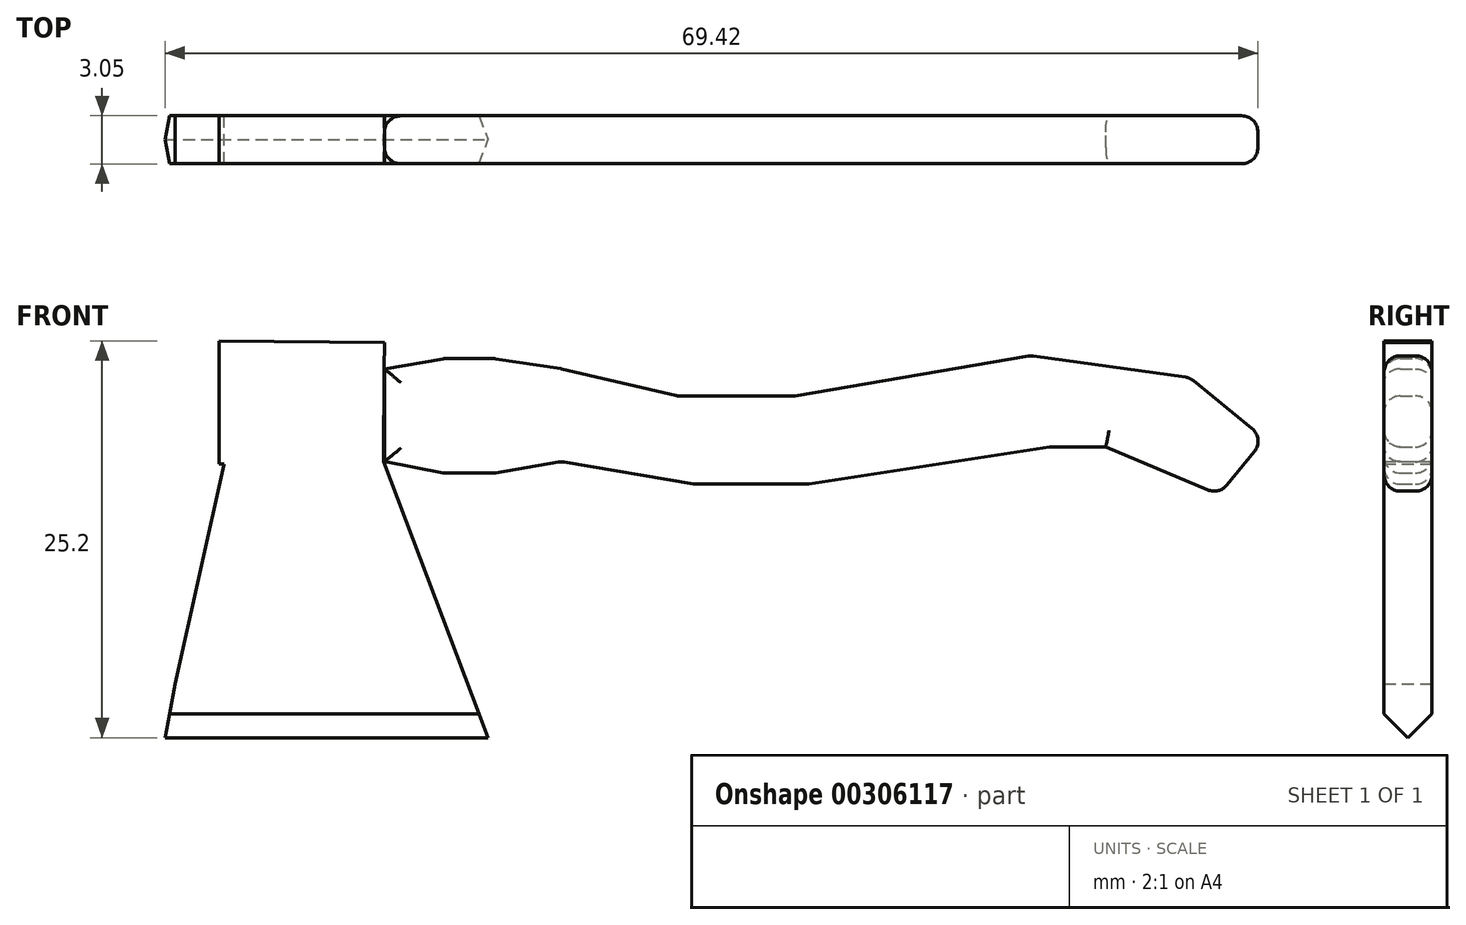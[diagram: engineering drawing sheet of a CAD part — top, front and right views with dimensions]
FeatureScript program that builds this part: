
annotation { "Feature Type Name" : "Feature", "Feature Type Description" : "" }
export const myFeature = defineFeature(function(context is Context, id is Id, definition is map)
    precondition{}
    {
        {
            var Q0;
            Q0=qCreatedBy(makeId("Front.planeOp"),FACE);
            var sketch = newSketch(context, id + "F0", { "sketchPlane" : qUnion([Q0])});
            skLineSegment(sketch, "E0", {"start": v(11.94, 3.92) * mm, "end": v(4.74, 6.95) * mm});
            skLineSegment(sketch, "E1", {"start": v(4.74, 6.95) * mm, "end": v(1.23, 6.95) * mm});
            skLineSegment(sketch, "E2", {"start": v(1.23, 6.95) * mm, "end": v(-14.2, 4.59) * mm});
            skLineSegment(sketch, "E3", {"start": v(-14.2, 4.59) * mm, "end": v(-21.36, 4.59) * mm});
            skLineSegment(sketch, "E4", {"start": v(-21.36, 4.59) * mm, "end": v(-29.85, 6.01) * mm});
            skLineSegment(sketch, "E5", {"start": v(-29.85, 6.01) * mm, "end": v(-34.1, 5.3) * mm});
            skLineSegment(sketch, "E6", {"start": v(-34.1, 5.3) * mm, "end": v(-37.26, 5.3) * mm});
            skLineSegment(sketch, "E7", {"start": v(-37.26, 5.3) * mm, "end": v(-41.07, 6.01) * mm});
            skLineSegment(sketch, "E8", {"start": v(-41.07, 6.01) * mm, "end": v(-41.07, 11.91) * mm});
            skLineSegment(sketch, "E9", {"start": v(-41.07, 11.91) * mm, "end": v(-37.26, 12.56) * mm});
            skLineSegment(sketch, "E10", {"start": v(-37.26, 12.56) * mm, "end": v(-34.1, 12.56) * mm});
            skLineSegment(sketch, "E11", {"start": v(-34.1, 12.56) * mm, "end": v(-29.85, 11.91) * mm});
            skLineSegment(sketch, "E12", {"start": v(-29.85, 11.91) * mm, "end": v(-22.44, 10.18) * mm});
            skLineSegment(sketch, "E13", {"start": v(-22.44, 10.18) * mm, "end": v(-15.1, 10.18) * mm});
            skLineSegment(sketch, "E14", {"start": v(-15.1, 10.18) * mm, "end": v(0, 12.75) * mm});
            skLineSegment(sketch, "E15", {"start": v(11.94, 3.92) * mm, "end": v(14.83, 7.45) * mm});
            skLineSegment(sketch, "E16", {"start": v(14.83, 7.45) * mm, "end": v(10.08, 11.34) * mm});
            skLineSegment(sketch, "E17", {"start": v(10.08, 11.34) * mm, "end": v(0, 12.75) * mm});
            skLineSegment(sketch, "E18", {"start": v(-41.09, 11.91) * mm, "end": v(-41.07, 13.58) * mm});
            skLineSegment(sketch, "E19", {"start": v(-41.07, 13.58) * mm, "end": v(-51.58, 13.68) * mm});
            skLineSegment(sketch, "E20", {"start": v(-51.58, 13.68) * mm, "end": v(-51.58, 5.88) * mm});
            skLineSegment(sketch, "E21", {"start": v(-51.58, 5.88) * mm, "end": v(-51.25, 5.88) * mm});
            skLineSegment(sketch, "E22", {"start": v(-51.25, 5.88) * mm, "end": v(-54.38, -8.11) * mm});
            skLineSegment(sketch, "E23", {"start": v(-54.38, -8.11) * mm, "end": v(-55.2, -12.54) * mm});
            skLineSegment(sketch, "E24", {"start": v(-55.2, -12.54) * mm, "end": v(-34.1, -12.54) * mm});
            skLineSegment(sketch, "E25", {"start": v(-34.1, -12.54) * mm, "end": v(-41.14, 6.01) * mm});
            skLineSegment(sketch, "E26", {"start": v(-41.14, 6.01) * mm, "end": v(-41.09, 11.91) * mm});
            skSolve(sketch);
        }
        {
            var Q0;
            Q0 = qSketchRegion(id + "F0", true);
            extrude(context, id + "F1", {"entities" : qUnion([Q0]), "depth" : 3.05 * mm});
        }
        {
            var Q0;
            Q0=makeQuery(id+"F1.opExtrude","CAP_EDGE",EDGE,{"disambiguationData":[OSD([sQuery(id+"F0.wireOp",EDGE,"E15")])],"isStart":false});
            var Q1;
            Q1=makeQuery(id+"F1.opExtrude","CAP_EDGE",EDGE,{"disambiguationData":[OSD([sQuery(id+"F0.wireOp",EDGE,"E15")])],"isStart":true});
            var Q2;
            Q2=makeQuery(id+"F1.opExtrude","CAP_EDGE",EDGE,{"disambiguationData":[OSD([sQuery(id+"F0.wireOp",EDGE,"E16")])],"isStart":true});
            var Q3;
            Q3=makeQuery(id+"F1.opExtrude","CAP_EDGE",EDGE,{"disambiguationData":[OSD([sQuery(id+"F0.wireOp",EDGE,"E16")])],"isStart":false});
            var Q4;
            Q4=makeQuery(id+"F1.opExtrude","SWEPT_EDGE",EDGE,{"disambiguationData":[OSD([sQuery(id+"F0.wireOp",EDGE,"E15"),sQuery(id+"F0.wireOp",EDGE,"E16")])]});
            var Q5;
            Q5=makeQuery(id+"F1.opExtrude","SWEPT_EDGE",EDGE,{"disambiguationData":[OSD([sQuery(id+"F0.wireOp",EDGE,"E0"),sQuery(id+"F0.wireOp",EDGE,"E15")])]});
            var Q6;
            Q6=makeQuery(id+"F1.opExtrude","CAP_EDGE",EDGE,{"disambiguationData":[OSD([sQuery(id+"F0.wireOp",EDGE,"E0")])],"isStart":false});
            var Q7;
            Q7=makeQuery(id+"F1.opExtrude","CAP_EDGE",EDGE,{"disambiguationData":[OSD([sQuery(id+"F0.wireOp",EDGE,"E1")])],"isStart":false});
            var Q8;
            Q8=makeQuery(id+"F1.opExtrude","CAP_EDGE",EDGE,{"disambiguationData":[OSD([sQuery(id+"F0.wireOp",EDGE,"E2")])],"isStart":false});
            var Q9;
            Q9=makeQuery(id+"F1.opExtrude","CAP_EDGE",EDGE,{"disambiguationData":[OSD([sQuery(id+"F0.wireOp",EDGE,"E14")])],"isStart":false});
            var Q10;
            Q10=makeQuery(id+"F1.opExtrude","CAP_EDGE",EDGE,{"disambiguationData":[OSD([sQuery(id+"F0.wireOp",EDGE,"E17")])],"isStart":false});
            var Q11;
            Q11=makeQuery(id+"F1.opExtrude","CAP_EDGE",EDGE,{"disambiguationData":[OSD([sQuery(id+"F0.wireOp",EDGE,"E17")])],"isStart":true});
            var Q12;
            Q12=makeQuery(id+"F1.opExtrude","SWEPT_EDGE",EDGE,{"disambiguationData":[OSD([sQuery(id+"F0.wireOp",EDGE,"E14"),sQuery(id+"F0.wireOp",EDGE,"E17")])]});
            var Q13;
            Q13=makeQuery(id+"F1.opExtrude","SWEPT_EDGE",EDGE,{"disambiguationData":[OSD([sQuery(id+"F0.wireOp",EDGE,"E16"),sQuery(id+"F0.wireOp",EDGE,"E17")])]});
            var Q14;
            Q14=makeQuery(id+"F1.opExtrude","SWEPT_FACE",FACE,{"disambiguationData":[OSD([sQuery(id+"F0.wireOp",EDGE,"E4")])]});
            var Q15;
            Q15=makeQuery(id+"F1.opExtrude","SWEPT_FACE",FACE,{"disambiguationData":[OSD([sQuery(id+"F0.wireOp",EDGE,"E3")])]});
            var Q16;
            Q16=makeQuery(id+"F1.opExtrude","SWEPT_FACE",FACE,{"disambiguationData":[OSD([sQuery(id+"F0.wireOp",EDGE,"E2")])]});
            var Q17;
            Q17=makeQuery(id+"F1.opExtrude","SWEPT_FACE",FACE,{"disambiguationData":[OSD([sQuery(id+"F0.wireOp",EDGE,"E6")])]});
            var Q18;
            Q18=makeQuery(id+"F1.opExtrude","CAP_FACE",FACE,{"disambiguationData":[OSD([sQuery(id+"F0.wireOp",EDGE,"E0"),sQuery(id+"F0.wireOp",EDGE,"E1"),sQuery(id+"F0.wireOp",EDGE,"E2"),sQuery(id+"F0.wireOp",EDGE,"E3"),sQuery(id+"F0.wireOp",EDGE,"E4"),sQuery(id+"F0.wireOp",EDGE,"E5"),sQuery(id+"F0.wireOp",EDGE,"E6"),sQuery(id+"F0.wireOp",EDGE,"E7"),sQuery(id+"F0.wireOp",EDGE,"E8"),sQuery(id+"F0.wireOp",EDGE,"E9"),sQuery(id+"F0.wireOp",EDGE,"E10"),sQuery(id+"F0.wireOp",EDGE,"E11"),sQuery(id+"F0.wireOp",EDGE,"E12"),sQuery(id+"F0.wireOp",EDGE,"E13"),sQuery(id+"F0.wireOp",EDGE,"E14"),sQuery(id+"F0.wireOp",EDGE,"E15"),sQuery(id+"F0.wireOp",EDGE,"E16"),sQuery(id+"F0.wireOp",EDGE,"E17")])],"isStart":false});
            var Q19;
            Q19=makeQuery(id+"F1.opExtrude","CAP_FACE",FACE,{"disambiguationData":[OSD([sQuery(id+"F0.wireOp",EDGE,"E0"),sQuery(id+"F0.wireOp",EDGE,"E1"),sQuery(id+"F0.wireOp",EDGE,"E2"),sQuery(id+"F0.wireOp",EDGE,"E3"),sQuery(id+"F0.wireOp",EDGE,"E4"),sQuery(id+"F0.wireOp",EDGE,"E5"),sQuery(id+"F0.wireOp",EDGE,"E6"),sQuery(id+"F0.wireOp",EDGE,"E7"),sQuery(id+"F0.wireOp",EDGE,"E8"),sQuery(id+"F0.wireOp",EDGE,"E9"),sQuery(id+"F0.wireOp",EDGE,"E10"),sQuery(id+"F0.wireOp",EDGE,"E11"),sQuery(id+"F0.wireOp",EDGE,"E12"),sQuery(id+"F0.wireOp",EDGE,"E13"),sQuery(id+"F0.wireOp",EDGE,"E14"),sQuery(id+"F0.wireOp",EDGE,"E15"),sQuery(id+"F0.wireOp",EDGE,"E16"),sQuery(id+"F0.wireOp",EDGE,"E17")])],"isStart":true});
            var Q20;
            Q20=makeQuery(id+"F1.opExtrude","SWEPT_EDGE",EDGE,{"disambiguationData":[OSD([sQuery(id+"F0.wireOp",EDGE,"E13"),sQuery(id+"F0.wireOp",EDGE,"E14")])]});
            var Q21;
            Q21=makeQuery(id+"F1.opExtrude","SWEPT_EDGE",EDGE,{"disambiguationData":[OSD([sQuery(id+"F0.wireOp",EDGE,"E12"),sQuery(id+"F0.wireOp",EDGE,"E13")])]});
            var Q22;
            Q22=makeQuery(id+"F1.opExtrude","SWEPT_EDGE",EDGE,{"disambiguationData":[OSD([sQuery(id+"F0.wireOp",EDGE,"E11"),sQuery(id+"F0.wireOp",EDGE,"E12")])]});
            var Q23;
            Q23=makeQuery(id+"F1.opExtrude","SWEPT_EDGE",EDGE,{"disambiguationData":[OSD([sQuery(id+"F0.wireOp",EDGE,"E10"),sQuery(id+"F0.wireOp",EDGE,"E11")])]});
            var Q24;
            Q24=makeQuery(id+"F1.opExtrude","SWEPT_EDGE",EDGE,{"disambiguationData":[OSD([sQuery(id+"F0.wireOp",EDGE,"E9"),sQuery(id+"F0.wireOp",EDGE,"E10")])]});
            fillet(context, id + "F2", {"entities" : qUnion([Q0, Q1, Q2, Q3, Q4, Q5, Q6, Q7, Q8, Q9, Q10, Q11, Q12, Q13, Q14, Q15, Q16, Q17, Q18, Q19, Q20, Q21, Q22, Q23, Q24]), "radius" : 1.04 * mm, "tangentPropagation" : true, "allowEdgeOverflow" : false});
        }
        {
            var Q0;
            Q0=makeQuery(id+"F1.opExtrude","CAP_EDGE",EDGE,{"disambiguationData":[OSD([sQuery(id+"F0.wireOp",EDGE,"E24")])],"isStart":true});
            var Q1;
            Q1=makeQuery(id+"F1.opExtrude","CAP_EDGE",EDGE,{"disambiguationData":[OSD([sQuery(id+"F0.wireOp",EDGE,"E24")])],"isStart":false});
            chamfer(context, id + "F3", {"entities" : qUnion([Q0, Q1]), "width" : 2.54 * mm, "tangentPropagation" : true});
        }
    });
